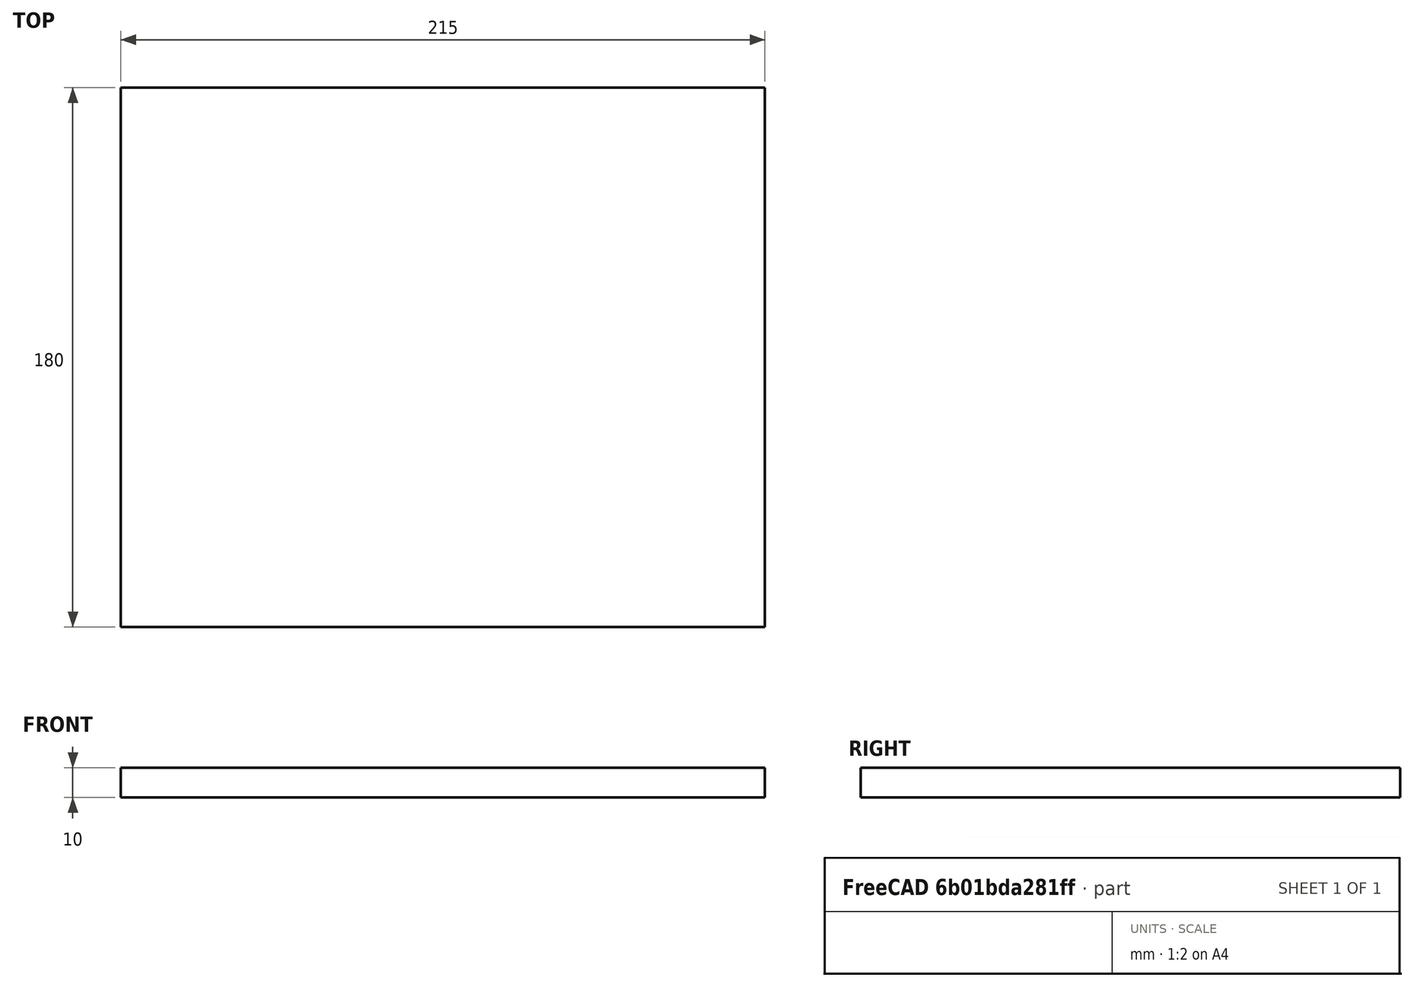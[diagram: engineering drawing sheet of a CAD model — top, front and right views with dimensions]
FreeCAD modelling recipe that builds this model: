
FCSTD DOCUMENT  (FreeCAD 0.18R4 (GitTag))
Label: BackMedium
License: All rights reserved
LicenseURL: http://en.wikipedia.org/wiki/All_rights_reserved
objects: Sketcher::SketchObject×1, PartDesign::Pad×1, PartDesign::Body×1
note: 4 computed .brp shape members not serialized (recipe doc carries the construction recipe); baked Part::Feature solids carry a one-line shape summary decoded from their .brp

FEATURE [Sketcher::SketchObject] Sketch
  MapMode = 5
  Support = -> [XY_Plane]
  sketch-geometry (4):
    g0: LineSegment StartX=0 StartY=0 StartZ=0 EndX=-215 EndY=0 EndZ=0
    g1: LineSegment StartX=-215 StartY=0 StartZ=0 EndX=-215 EndY=180 EndZ=0
    g2: LineSegment StartX=-215 StartY=180 StartZ=0 EndX=0 EndY=180 EndZ=0
    g3: LineSegment StartX=0 StartY=180 StartZ=0 EndX=0 EndY=0 EndZ=0
  constraints (11):
    c: Coincident(g0,g1)
    c: Coincident(g1,g2)
    c: Coincident(g2,g3)
    c: Coincident(g3,g0)
    c: Horizontal(g0)
    c: Horizontal(g2)
    c: Vertical(g1)
    c: Vertical(g3)
    c: Distance(g2) = 215
    c: Distance(g3) = 180
    c: Coincident(g0,g-1)
FEATURE [PartDesign::Pad] Pad
  Length = 10
  Length2 = 100
  Profile = -> Sketch
  Type = 0
FEATURE [PartDesign::Body] Body
  Group = -> [Sketch,Pad]
  Origin = -> Origin
  Tip = -> Pad
